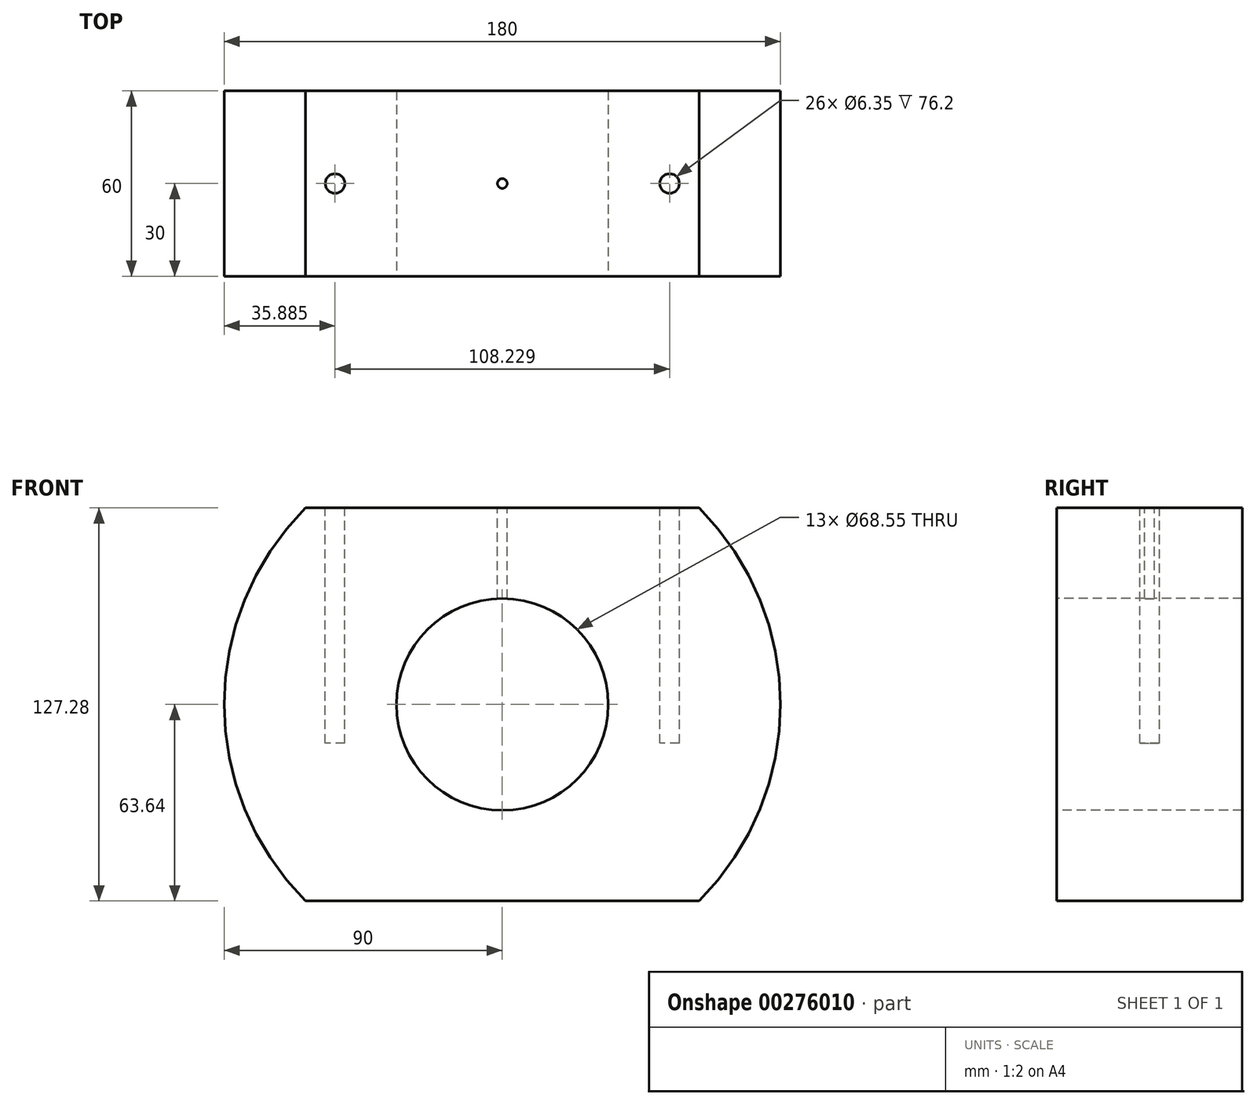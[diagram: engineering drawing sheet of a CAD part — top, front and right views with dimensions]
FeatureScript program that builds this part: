
annotation { "Feature Type Name" : "Feature", "Feature Type Description" : "" }
export const myFeature = defineFeature(function(context is Context, id is Id, definition is map)
    precondition{}
    {
        {
            var Q0;
            Q0=qCreatedBy(makeId("Front.planeOp"),FACE);
            var sketch = newSketch(context, id + "F0", { "sketchPlane" : qUnion([Q0])});
            skCircle(sketch, "E0", {"center": v(0, 0) * mm, "radius": 90 * mm});
            skSolve(sketch);
        }
        {
            var Q0;
            Q0=makeQuery(id+"F0.imprint","IMPRINT",FACE,{"disambiguationData":[TD([[makeQuery(id+"F0.imprint","IMPRINT",EDGE,{"derivedFrom":sQuery(id+"F0.wireOp",EDGE,"E0")}),1.0]])]});
            extrude(context, id + "F1", {"entities" : qUnion([Q0]), "endBound" : BoundingType.SYMMETRIC, "depth" : 60 * mm});
        }
        {
            var Q0;
            Q0=makeQuery(id+"F1.opExtrude","CAP_FACE",FACE,{"disambiguationData":[OSD([sQuery(id+"F0.wireOp",EDGE,"E0")])],"isStart":false});
            var sketch = newSketch(context, id + "F2", { "sketchPlane" : qUnion([Q0])});
            skLineSegment(sketch, "E1.top", {"start": v(63.64, -63.64) * mm, "end": v(-63.64, -63.64) * mm});
            skLineSegment(sketch, "E1.left", {"start": v(63.64, 63.64) * mm, "end": v(63.64, -63.64) * mm});
            skLineSegment(sketch, "E1.right", {"start": v(-63.64, 63.64) * mm, "end": v(-63.64, -63.64) * mm});
            skPoint(sketch, "E1.middle", {"position": v(0, 0) * mm});
            skLineSegment(sketch, "E2", {"start": v(-63.64, 63.64) * mm, "end": v(63.64, 63.64) * mm});
            skSolve(sketch);
        }
        {
            var Q0;
            {var subQ0=sQuery(id+"F2.wireOp",EDGE,"E1.top");Q0=makeQuery(id+"F2.imprint","IMPRINT",FACE,{"disambiguationData":[TD([[makeQuery(id+"F2.imprint","IMPRINT",EDGE,{"derivedFrom":subQ0}),1.0]])]});}
            var Q1;
            {var subQ0=sQuery(id+"F2.wireOp",EDGE,"E2");Q1=makeQuery(id+"F2.imprint","IMPRINT",FACE,{"disambiguationData":[TD([[makeQuery(id+"F2.imprint","IMPRINT",EDGE,{"derivedFrom":subQ0}),1.0]])]});}
            extrude(context, id + "F3", {"entities" : qUnion([Q0, Q1]), "operationType" : NewBodyOperationType.REMOVE, "endBound" : BoundingType.THROUGH_ALL, "oppositeDirection" : true, "depth" : 25.4 * mm});
        }
        {
            var Q0;
            Q0=makeQuery(id+"F1.opExtrude","CAP_FACE",FACE,{"disambiguationData":[OSD([sQuery(id+"F0.wireOp",EDGE,"E0")])],"isStart":false});
            var sketch = newSketch(context, id + "F4", { "sketchPlane" : qUnion([Q0])});
            skCircle(sketch, "E3", {"center": v(0, 0) * mm, "radius": 34.27 * mm});
            skSolve(sketch);
        }
        {
            var Q0;
            Q0=makeQuery(id+"F4.imprint","IMPRINT",FACE,{"disambiguationData":[TD([[makeQuery(id+"F4.imprint","IMPRINT",EDGE,{"derivedFrom":sQuery(id+"F4.wireOp",EDGE,"E3")}),1.0]])]});
            extrude(context, id + "F5", {"entities" : qUnion([Q0]), "operationType" : NewBodyOperationType.REMOVE, "endBound" : BoundingType.THROUGH_ALL, "oppositeDirection" : true, "depth" : 25.4 * mm});
        }
        {
            var Q0;
            Q0=makeQuery(id+"F3.boolean.opBoolean","COPY",FACE,{"derivedFrom":makeQuery(id+"F3.opExtrude","SWEPT_FACE",FACE,{"disambiguationData":[OSD([sQuery(id+"F2.wireOp",EDGE,"E2")])]})});
            var sketch = newSketch(context, id + "F6", { "sketchPlane" : qUnion([Q0])});
            skCircle(sketch, "E4", {"center": v(0, 0) * mm, "radius": 1.59 * mm});
            skCircle(sketch, "E5", {"center": v(54.11, 0) * mm, "radius": 3.18 * mm});
            skCircle(sketch, "E6", {"center": v(-54.11, 0) * mm, "radius": 3.18 * mm});
            skSolve(sketch);
        }
        {
            var Q0;
            Q0=makeQuery(id+"F6.imprint","IMPRINT",FACE,{"disambiguationData":[TD([[makeQuery(id+"F6.imprint","IMPRINT",EDGE,{"derivedFrom":sQuery(id+"F6.wireOp",EDGE,"E6")}),1.0]])]});
            var Q1;
            Q1=makeQuery(id+"F6.imprint","IMPRINT",FACE,{"disambiguationData":[TD([[makeQuery(id+"F6.imprint","IMPRINT",EDGE,{"derivedFrom":sQuery(id+"F6.wireOp",EDGE,"E4")}),1.0]])]});
            var Q2;
            Q2=makeQuery(id+"F6.imprint","IMPRINT",FACE,{"disambiguationData":[TD([[makeQuery(id+"F6.imprint","IMPRINT",EDGE,{"derivedFrom":sQuery(id+"F6.wireOp",EDGE,"E5")}),1.0]])]});
            extrude(context, id + "F7", {"entities" : qUnion([Q0, Q1, Q2]), "operationType" : NewBodyOperationType.REMOVE, "oppositeDirection" : true, "depth" : 76.2 * mm});
        }
    });
